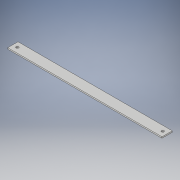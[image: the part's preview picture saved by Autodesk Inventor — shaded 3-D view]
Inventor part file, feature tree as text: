
AUTODESK INVENTOR PART (.ipt)
format: ipt  version: 2017 (Build 210142000, 142)  size: 104,448 bytes
history: native  units: in
note: dims shown in document units (in); Inventor stores cm internally (conversion verified against a paired STEP export)
features: extrude x2, sketch x2
ambient origin geometry x8: Origin, YZ Plane, XZ Plane, XY Plane, X Axis, Y Axis, Z Axis, Center Point
bodies: Solid1 (feature_tree)
feature tree (4):
  extrude  "Extrusion1"  Depth=1.0in
  extrude  "Extrusion2"  Depth=15.0in
  sketch  "Sketch1"  dims[d0=0.128in d1=1.0in]
  sketch  "Sketch2"  dims[d2=15.0in d3=0.0in d4=0.25in d5=7.0711in d6=15.0in d7=0.0in]
